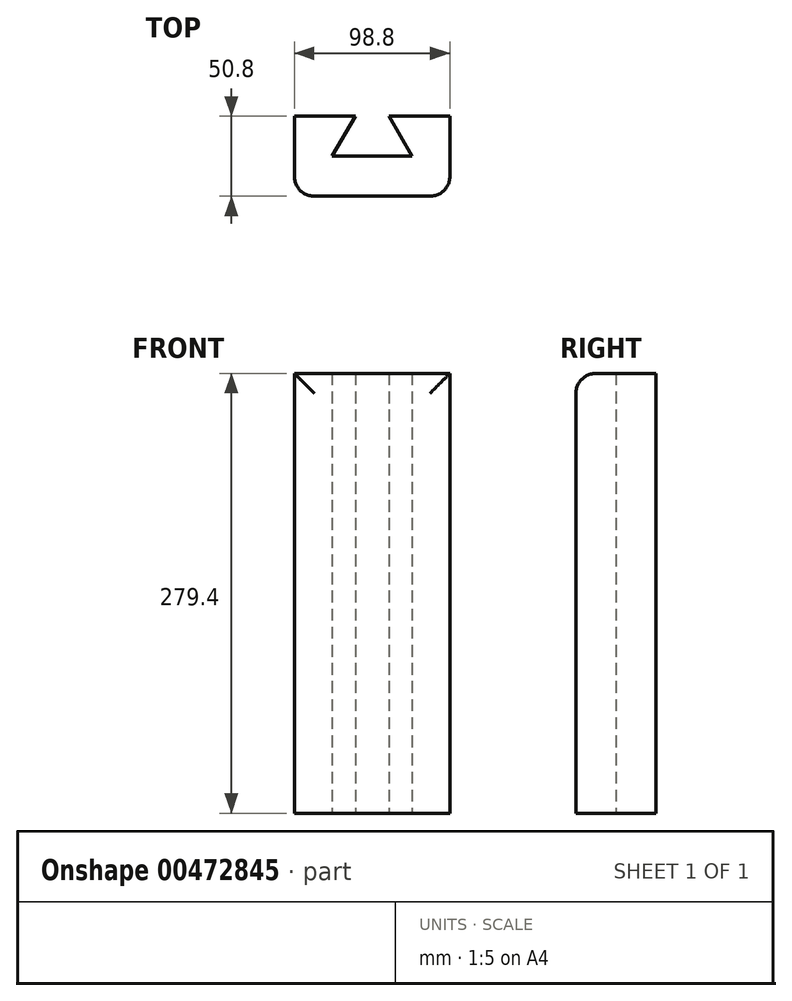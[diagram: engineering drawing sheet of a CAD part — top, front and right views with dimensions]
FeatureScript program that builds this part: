
annotation { "Feature Type Name" : "Feature", "Feature Type Description" : "" }
export const myFeature = defineFeature(function(context is Context, id is Id, definition is map)
    precondition{}
    {
        {
            var Q0;
            Q0=qCreatedBy(makeId("Top.planeOp"),FACE);
            var sketch = newSketch(context, id + "F0", { "sketchPlane" : qUnion([Q0])});
            skLineSegment(sketch, "E0.bottom", {"start": v(49.4, 25.4) * mm, "end": v(10.78, 25.4) * mm});
            skLineSegment(sketch, "E0.top", {"start": v(36.7, -25.4) * mm, "end": v(-36.7, -25.4) * mm});
            skLineSegment(sketch, "E0.left", {"start": v(49.4, 25.4) * mm, "end": v(49.4, -12.7) * mm});
            skLineSegment(sketch, "E0.right", {"start": v(-49.4, 25.4) * mm, "end": v(-49.4, -12.7) * mm});
            skPoint(sketch, "E0.middle", {"position": v(0, 0) * mm});
            skLineSegment(sketch, "E1", {"start": v(-10.69, 25.4) * mm, "end": v(-25.35, 0) * mm});
            skLineSegment(sketch, "E2", {"start": v(-25.35, 0) * mm, "end": v(25.45, 0) * mm});
            skLineSegment(sketch, "E3", {"start": v(25.45, 0) * mm, "end": v(10.78, 25.4) * mm});
            skLineSegment(sketch, "E4.trimOffspring", {"start": v(-10.69, 25.4) * mm, "end": v(-49.4, 25.4) * mm});
            skPoint(sketch, "E5.visualSharp", {"position": v(-49.4, -25.4) * mm});
            skArc(sketch, "E5.filletArc", {"start": v(-49.4, -12.7) * mm, "mid": v(-45.68, -21.68) * mm, "end": v(-36.7, -25.4) * mm});
            skPoint(sketch, "E6.visualSharp", {"position": v(49.4, -25.4) * mm});
            skArc(sketch, "E6.filletArc", {"start": v(36.7, -25.4) * mm, "mid": v(45.68, -21.68) * mm, "end": v(49.4, -12.7) * mm});
            skSolve(sketch);
        }
        {
            var Q0;
            Q0 = qSketchRegion(id + "F0", true);
            extrude(context, id + "F1", {"entities" : qUnion([Q0]), "depth" : 279.4 * mm});
        }
        {
            var Q0;
            Q0=makeQuery(id+"F1.opExtrude","CAP_EDGE",EDGE,{"disambiguationData":[OSD([sQuery(id+"F0.wireOp",EDGE,"E0.top")])],"isStart":false});
            fillet(context, id + "F2", {"entities" : qUnion([Q0]), "radius" : 12.7 * mm, "allowEdgeOverflow" : false});
        }
    });
